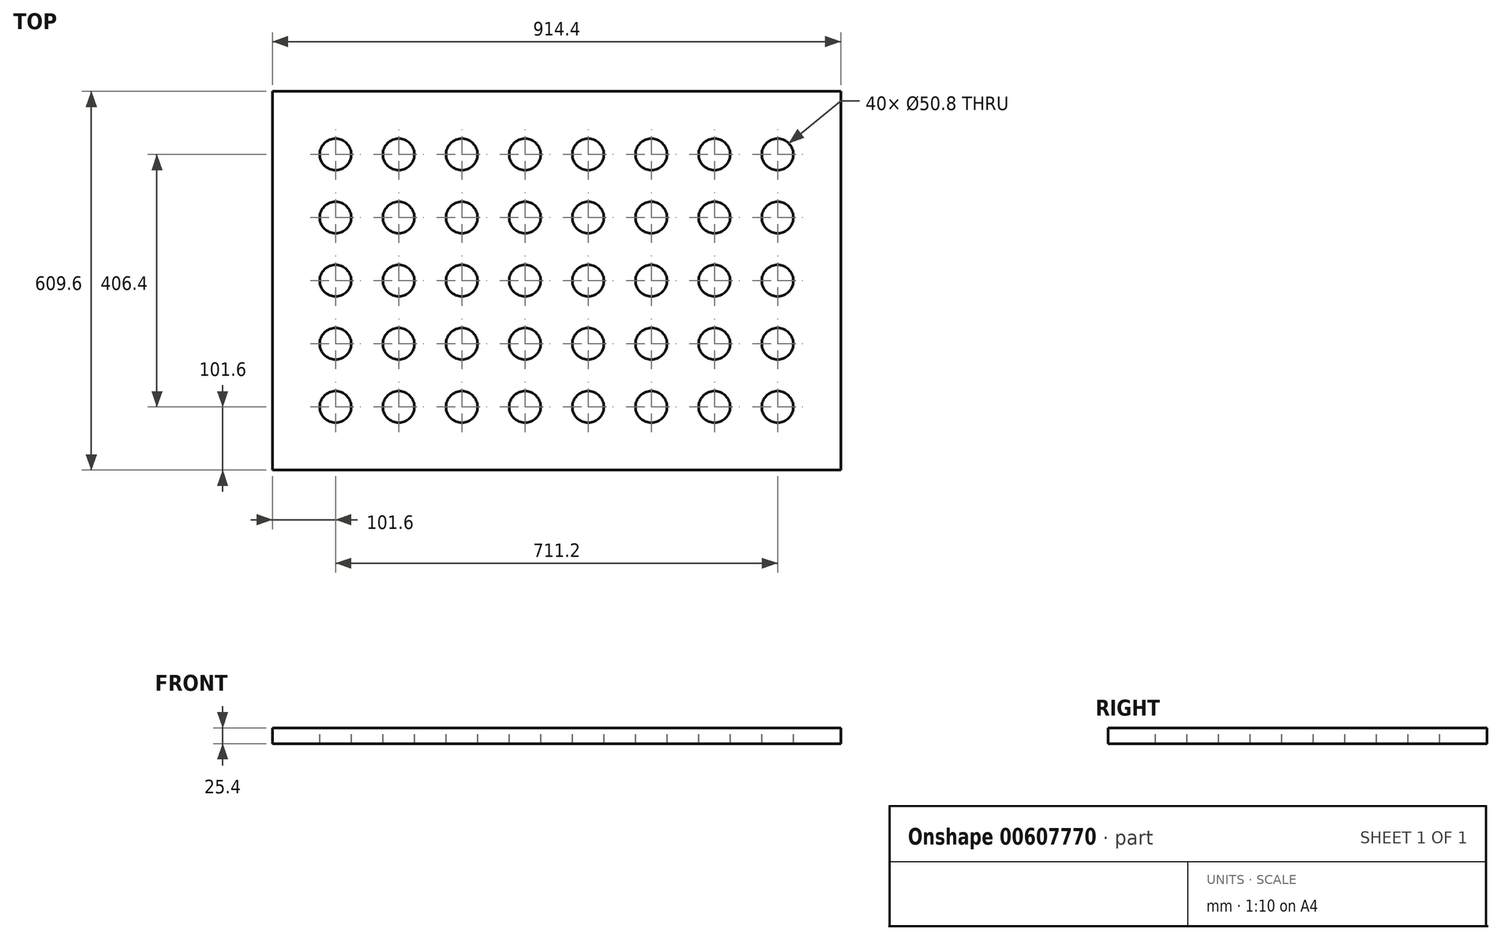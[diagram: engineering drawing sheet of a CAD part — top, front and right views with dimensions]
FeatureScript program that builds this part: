
annotation { "Feature Type Name" : "Feature", "Feature Type Description" : "" }
export const myFeature = defineFeature(function(context is Context, id is Id, definition is map)
    precondition{}
    {
        {
            var Q0;
            Q0=qCreatedBy(makeId("Top.planeOp"),FACE);
            var sketch = newSketch(context, id + "F0", { "sketchPlane" : qUnion([Q0])});
            skLineSegment(sketch, "E0.bottom", {"start": v(457.2, 304.8) * mm, "end": v(-457.2, 304.8) * mm});
            skLineSegment(sketch, "E0.top", {"start": v(457.2, -304.8) * mm, "end": v(-457.2, -304.8) * mm});
            skLineSegment(sketch, "E0.left", {"start": v(457.2, 304.8) * mm, "end": v(457.2, -304.8) * mm});
            skLineSegment(sketch, "E0.right", {"start": v(-457.2, 304.8) * mm, "end": v(-457.2, -304.8) * mm});
            skPoint(sketch, "E0.middle", {"position": v(0, 0) * mm});
            skSolve(sketch);
        }
        {
            var Q0;
            Q0=makeQuery(id+"F0.imprint","IMPRINT",FACE,{"disambiguationData":[TD([[makeQuery(id+"F0.imprint","IMPRINT",EDGE,{"derivedFrom":sQuery(id+"F0.wireOp",EDGE,"E0.bottom")}),1.0]])]});
            extrude(context, id + "F1", {"entities" : qUnion([Q0]), "depth" : 25.4 * mm, "offsetDistance" : 25.4 * mm});
        }
        {
            var Q0;
            Q0=makeQuery(id+"F1.opExtrude","CAP_FACE",FACE,{"disambiguationData":[OSD([sQuery(id+"F0.wireOp",EDGE,"E0.bottom"),sQuery(id+"F0.wireOp",EDGE,"E0.top"),sQuery(id+"F0.wireOp",EDGE,"E0.left"),sQuery(id+"F0.wireOp",EDGE,"E0.right")])],"isStart":false});
            var sketch = newSketch(context, id + "F2", { "sketchPlane" : qUnion([Q0])});
            skCircle(sketch, "E1", {"center": v(-355.6, -203.2) * mm, "radius": 25.4 * mm});
            skCircle(sketch, "E2.1.0.0", {"center": v(-254, -203.2) * mm, "radius": 25.4 * mm});
            skCircle(sketch, "E2.2.0.0", {"center": v(-152.4, -203.2) * mm, "radius": 25.4 * mm});
            skCircle(sketch, "E2.3.0.0", {"center": v(-50.8, -203.2) * mm, "radius": 25.4 * mm});
            skCircle(sketch, "E2.4.0.0", {"center": v(50.8, -203.2) * mm, "radius": 25.4 * mm});
            skCircle(sketch, "E2.5.0.0", {"center": v(152.4, -203.2) * mm, "radius": 25.4 * mm});
            skCircle(sketch, "E2.6.0.0", {"center": v(254, -203.2) * mm, "radius": 25.4 * mm});
            skCircle(sketch, "E2.7.0.0", {"center": v(355.6, -203.2) * mm, "radius": 25.4 * mm});
            skLineSegment(sketch, "E2.direction1", {"start": v(-355.6, -203.2) * mm, "end": v(-254, -203.2) * mm, "construction": true});
            skCircle(sketch, "E3.0.1.0", {"center": v(-355.6, -101.6) * mm, "radius": 25.4 * mm});
            skCircle(sketch, "E3.0.2.0", {"center": v(-355.6, 0) * mm, "radius": 25.4 * mm});
            skCircle(sketch, "E3.0.3.0", {"center": v(-355.6, 101.6) * mm, "radius": 25.4 * mm});
            skCircle(sketch, "E3.0.4.0", {"center": v(-355.6, 203.2) * mm, "radius": 25.4 * mm});
            skCircle(sketch, "E3.1.1.0", {"center": v(-254, -101.6) * mm, "radius": 25.4 * mm});
            skCircle(sketch, "E3.1.2.0", {"center": v(-254, 0) * mm, "radius": 25.4 * mm});
            skCircle(sketch, "E3.1.3.0", {"center": v(-254, 101.6) * mm, "radius": 25.4 * mm});
            skCircle(sketch, "E3.1.4.0", {"center": v(-254, 203.2) * mm, "radius": 25.4 * mm});
            skCircle(sketch, "E3.2.1.0", {"center": v(-152.4, -101.6) * mm, "radius": 25.4 * mm});
            skCircle(sketch, "E3.2.2.0", {"center": v(-152.4, 0) * mm, "radius": 25.4 * mm});
            skCircle(sketch, "E3.2.3.0", {"center": v(-152.4, 101.6) * mm, "radius": 25.4 * mm});
            skCircle(sketch, "E3.2.4.0", {"center": v(-152.4, 203.2) * mm, "radius": 25.4 * mm});
            skCircle(sketch, "E3.3.1.0", {"center": v(-50.8, -101.6) * mm, "radius": 25.4 * mm});
            skCircle(sketch, "E3.3.2.0", {"center": v(-50.8, 0) * mm, "radius": 25.4 * mm});
            skCircle(sketch, "E3.3.3.0", {"center": v(-50.8, 101.6) * mm, "radius": 25.4 * mm});
            skCircle(sketch, "E3.3.4.0", {"center": v(-50.8, 203.2) * mm, "radius": 25.4 * mm});
            skCircle(sketch, "E3.4.1.0", {"center": v(50.8, -101.6) * mm, "radius": 25.4 * mm});
            skCircle(sketch, "E3.4.2.0", {"center": v(50.8, 0) * mm, "radius": 25.4 * mm});
            skCircle(sketch, "E3.4.3.0", {"center": v(50.8, 101.6) * mm, "radius": 25.4 * mm});
            skCircle(sketch, "E3.4.4.0", {"center": v(50.8, 203.2) * mm, "radius": 25.4 * mm});
            skCircle(sketch, "E3.5.1.0", {"center": v(152.4, -101.6) * mm, "radius": 25.4 * mm});
            skCircle(sketch, "E3.5.2.0", {"center": v(152.4, 0) * mm, "radius": 25.4 * mm});
            skCircle(sketch, "E3.5.3.0", {"center": v(152.4, 101.6) * mm, "radius": 25.4 * mm});
            skCircle(sketch, "E3.5.4.0", {"center": v(152.4, 203.2) * mm, "radius": 25.4 * mm});
            skCircle(sketch, "E3.6.1.0", {"center": v(254, -101.6) * mm, "radius": 25.4 * mm});
            skCircle(sketch, "E3.6.2.0", {"center": v(254, 0) * mm, "radius": 25.4 * mm});
            skCircle(sketch, "E3.6.3.0", {"center": v(254, 101.6) * mm, "radius": 25.4 * mm});
            skCircle(sketch, "E3.6.4.0", {"center": v(254, 203.2) * mm, "radius": 25.4 * mm});
            skCircle(sketch, "E3.7.1.0", {"center": v(355.6, -101.6) * mm, "radius": 25.4 * mm});
            skCircle(sketch, "E3.7.2.0", {"center": v(355.6, 0) * mm, "radius": 25.4 * mm});
            skCircle(sketch, "E3.7.3.0", {"center": v(355.6, 101.6) * mm, "radius": 25.4 * mm});
            skCircle(sketch, "E3.7.4.0", {"center": v(355.6, 203.2) * mm, "radius": 25.4 * mm});
            skLineSegment(sketch, "E3.direction2", {"start": v(-355.6, -203.2) * mm, "end": v(-355.6, -101.6) * mm, "construction": true});
            skSolve(sketch);
        }
        {
            var Q0;
            Q0 = qSketchRegion(id + "F2", true);
            extrude(context, id + "F3", {"entities" : qUnion([Q0]), "operationType" : NewBodyOperationType.REMOVE, "endBound" : BoundingType.UP_TO_NEXT, "oppositeDirection" : true, "depth" : 25.4 * mm, "offsetDistance" : 25.4 * mm});
        }
    });
